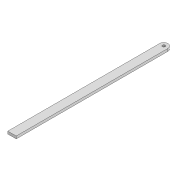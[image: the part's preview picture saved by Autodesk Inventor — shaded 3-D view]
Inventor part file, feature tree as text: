
AUTODESK INVENTOR PART (.ipt)
format: ipt  version: 2022 (Build 260153000, 153)  size: 100,352 bytes
history: native  units: mm
features: extrude x2, sketch x2
ambient origin geometry x8: Origin, YZ Plane, XZ Plane, XY Plane, X Axis, Y Axis, Z Axis, Center Point
bodies: Solid1 (feature_tree)
feature tree (4):
  extrude  "Extrusion1"  Depth=3.3mm
  extrude  "Extrusion2"  Depth=355.998mm
  sketch  "Sketch1"  dims[d0=3.3mm d1=3.3mm]
  sketch  "Sketch2"  dims[d2=10.0mm d3=355.998mm d6=3.0mm d7=0.0mm d14=3.3mm d15=57.376mm d16=10.0mm d17=0.0mm]
